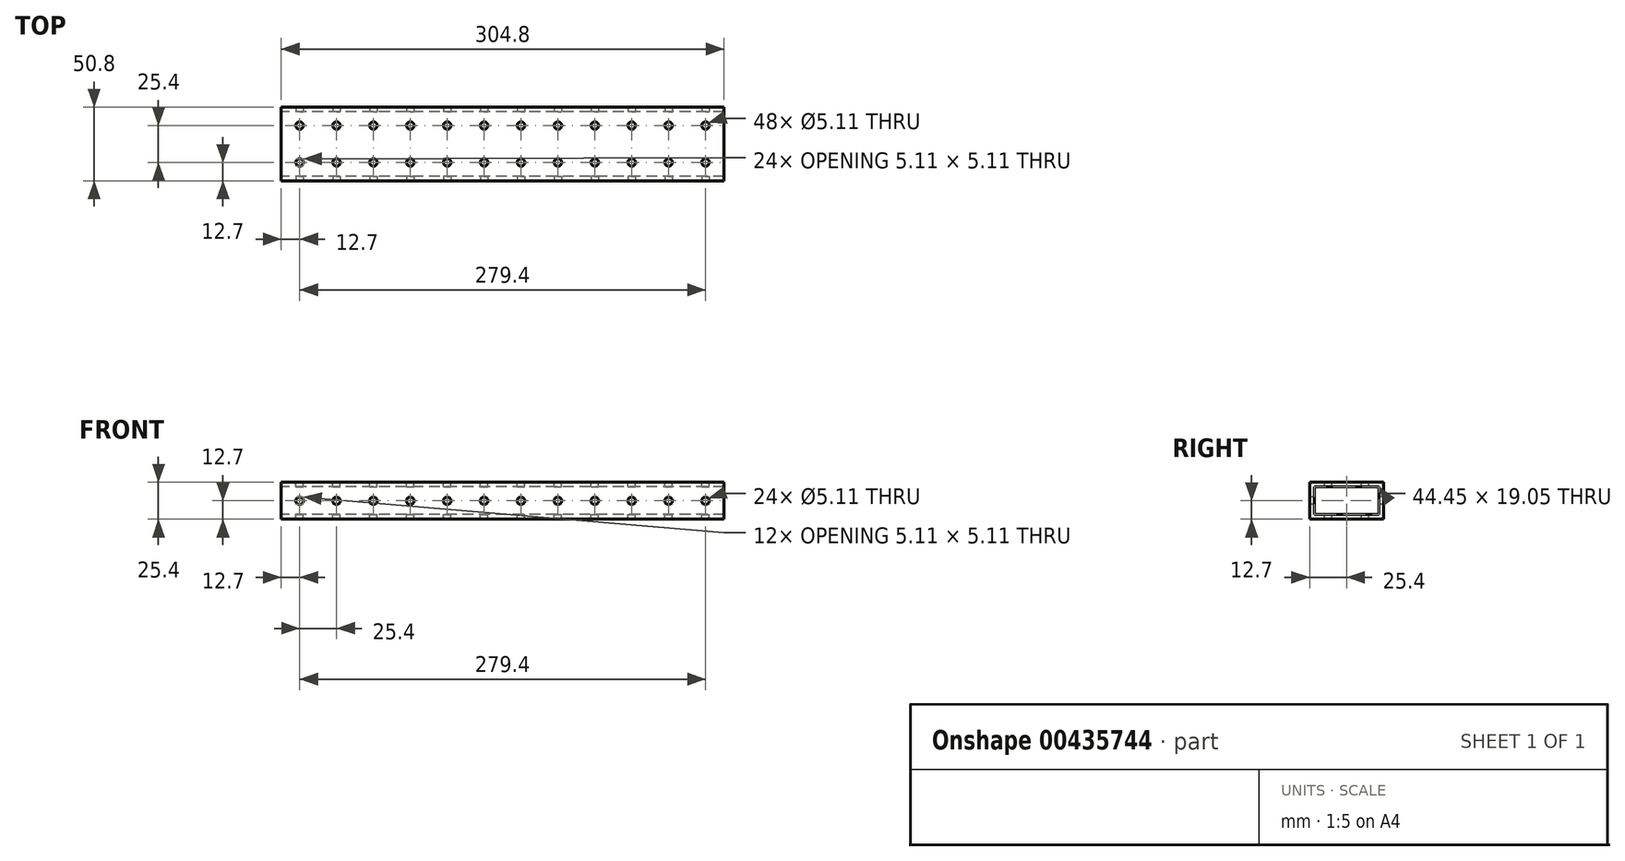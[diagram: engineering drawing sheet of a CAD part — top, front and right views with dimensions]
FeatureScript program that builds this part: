
annotation { "Feature Type Name" : "Feature", "Feature Type Description" : "" }
export const myFeature = defineFeature(function(context is Context, id is Id, definition is map)
    precondition{}
    {
        {
            var Q0;
            Q0=qCreatedBy(makeId("Right.planeOp"),FACE);
            var sketch = newSketch(context, id + "F0", { "sketchPlane" : qUnion([Q0])});
            skLineSegment(sketch, "E0.bottom", {"start": v(-25.4, -12.7) * mm, "end": v(25.4, -12.7) * mm});
            skLineSegment(sketch, "E0.top", {"start": v(-25.4, 12.7) * mm, "end": v(25.4, 12.7) * mm});
            skLineSegment(sketch, "E0.left", {"start": v(-25.4, -12.7) * mm, "end": v(-25.4, 12.7) * mm});
            skLineSegment(sketch, "E0.right", {"start": v(25.4, -12.7) * mm, "end": v(25.4, 12.7) * mm});
            skPoint(sketch, "E0.middle", {"position": v(0, 0) * mm});
            skLineSegment(sketch, "E1.bottom", {"start": v(22.23, 9.53) * mm, "end": v(-22.23, 9.53) * mm});
            skLineSegment(sketch, "E1.top", {"start": v(22.23, -9.53) * mm, "end": v(-22.23, -9.53) * mm});
            skLineSegment(sketch, "E1.left", {"start": v(22.23, 9.53) * mm, "end": v(22.23, -9.53) * mm});
            skLineSegment(sketch, "E1.right", {"start": v(-22.23, 9.53) * mm, "end": v(-22.23, -9.53) * mm});
            skSolve(sketch);
        }
        {
            var Q0;
            Q0=makeQuery(id+"F0.imprint","IMPRINT",FACE,{"disambiguationData":[TD([[makeQuery(id+"F0.imprint","IMPRINT",EDGE,{"derivedFrom":sQuery(id+"F0.wireOp",EDGE,"E0.bottom")}),1.0]])]});
            extrude(context, id + "F1", {"entities" : qUnion([Q0]), "depth" : 304.8 * mm});
        }
        {
            var Q0;
            Q0=makeQuery(id+"F1.opExtrude","SWEPT_FACE",FACE,{"disambiguationData":[OSD([sQuery(id+"F0.wireOp",EDGE,"E0.left")])]});
            var sketch = newSketch(context, id + "F2", { "sketchPlane" : qUnion([Q0])});
            skCircle(sketch, "E2", {"center": v(12.7, 0) * mm, "radius": 2.55 * mm});
            skCircle(sketch, "E3.1.0.0", {"center": v(38.1, 0) * mm, "radius": 2.55 * mm});
            skCircle(sketch, "E3.1.1.0", {"center": v(38.1, 0) * mm, "radius": 2.55 * mm});
            skCircle(sketch, "E3.2.0.0", {"center": v(63.5, 0) * mm, "radius": 2.55 * mm});
            skCircle(sketch, "E3.2.1.0", {"center": v(63.5, 0) * mm, "radius": 2.55 * mm});
            skCircle(sketch, "E3.3.0.0", {"center": v(88.9, 0) * mm, "radius": 2.55 * mm});
            skCircle(sketch, "E3.3.1.0", {"center": v(88.9, 0) * mm, "radius": 2.55 * mm});
            skCircle(sketch, "E3.4.0.0", {"center": v(114.3, 0) * mm, "radius": 2.55 * mm});
            skCircle(sketch, "E3.4.1.0", {"center": v(114.3, 0) * mm, "radius": 2.55 * mm});
            skCircle(sketch, "E3.5.0.0", {"center": v(139.7, 0) * mm, "radius": 2.55 * mm});
            skCircle(sketch, "E3.5.1.0", {"center": v(139.7, 0) * mm, "radius": 2.55 * mm});
            skCircle(sketch, "E3.6.0.0", {"center": v(165.1, 0) * mm, "radius": 2.55 * mm});
            skCircle(sketch, "E3.6.1.0", {"center": v(165.1, 0) * mm, "radius": 2.55 * mm});
            skCircle(sketch, "E3.7.0.0", {"center": v(190.5, 0) * mm, "radius": 2.55 * mm});
            skCircle(sketch, "E3.7.1.0", {"center": v(190.5, 0) * mm, "radius": 2.55 * mm});
            skCircle(sketch, "E3.8.0.0", {"center": v(215.9, 0) * mm, "radius": 2.55 * mm});
            skCircle(sketch, "E3.8.1.0", {"center": v(215.9, 0) * mm, "radius": 2.55 * mm});
            skCircle(sketch, "E3.9.0.0", {"center": v(241.3, 0) * mm, "radius": 2.55 * mm});
            skCircle(sketch, "E3.9.1.0", {"center": v(241.3, 0) * mm, "radius": 2.55 * mm});
            skCircle(sketch, "E3.10.0.0", {"center": v(266.7, 0) * mm, "radius": 2.55 * mm});
            skCircle(sketch, "E3.10.1.0", {"center": v(266.7, 0) * mm, "radius": 2.55 * mm});
            skCircle(sketch, "E3.11.0.0", {"center": v(292.1, 0) * mm, "radius": 2.55 * mm});
            skCircle(sketch, "E3.11.1.0", {"center": v(292.1, 0) * mm, "radius": 2.55 * mm});
            skLineSegment(sketch, "E3.direction1", {"start": v(12.7, 0) * mm, "end": v(38.1, 0) * mm, "construction": true});
            skLineSegment(sketch, "E3.direction2", {"start": v(12.7, 0) * mm, "end": v(12.7, 0) * mm});
            skSolve(sketch);
        }
        {
            var Q0;
            Q0=sQuery(id+"F2.wireOp",VERTEX,"E3.8.0.0.center");
            var Q1;
            Q1=sQuery(id+"F2.wireOp",VERTEX,"E3.16.0.0.center");
            var Q2;
            Q2=sQuery(id+"F2.wireOp",VERTEX,"E3.2.1.0.center");
            var Q3;
            Q3=sQuery(id+"F2.wireOp",VERTEX,"E3.3.0.0.center");
            var Q4;
            Q4=sQuery(id+"F2.wireOp",VERTEX,"E3.6.1.0.center");
            var Q5;
            Q5=sQuery(id+"F2.wireOp",VERTEX,"E3.direction1.end");
            var Q6;
            Q6=sQuery(id+"F2.wireOp",VERTEX,"E2.center");
            var Q7;
            Q7=sQuery(id+"F2.wireOp",VERTEX,"E3.4.0.0.center");
            var Q8;
            Q8=sQuery(id+"F2.wireOp",VERTEX,"E3.11.0.0.center");
            var Q9;
            Q9=sQuery(id+"F2.wireOp",VERTEX,"E3.19.0.0.center");
            var Q10;
            Q10=sQuery(id+"F2.wireOp",VERTEX,"E3.5.0.0.center");
            var Q11;
            Q11=sQuery(id+"F2.wireOp",VERTEX,"E3.22.0.0.center");
            var Q12;
            Q12=sQuery(id+"F2.wireOp",VERTEX,"E3.14.0.0.center");
            var Q13;
            Q13=sQuery(id+"F2.wireOp",VERTEX,"E3.21.1.0.center");
            var Q14;
            Q14=sQuery(id+"F2.wireOp",VERTEX,"E3.9.0.0.center");
            var Q15;
            Q15=sQuery(id+"F2.wireOp",VERTEX,"E3.17.0.0.center");
            var Q16;
            Q16=sQuery(id+"F2.wireOp",VERTEX,"E3.13.1.0.center");
            var Q17;
            Q17=sQuery(id+"F2.wireOp",VERTEX,"E3.7.0.0.center");
            var Q18;
            Q18=sQuery(id+"F2.wireOp",VERTEX,"E3.15.0.0.center");
            var Q19;
            Q19=sQuery(id+"F2.wireOp",VERTEX,"E3.12.1.0.center");
            var Q20;
            Q20=sQuery(id+"F2.wireOp",VERTEX,"E3.20.1.0.center");
            var Q21;
            Q21=sQuery(id+"F2.wireOp",VERTEX,"E3.10.1.0.center");
            var Q22;
            Q22=sQuery(id+"F2.wireOp",VERTEX,"E3.18.1.0.center");
            var Q23;
            Q23=makeQuery(id+"F1.opExtrude","SWEPT_BODY",BODY,{"disambiguationData":[OSD([sQuery(id+"F0.wireOp",EDGE,"E0.bottom"),sQuery(id+"F0.wireOp",EDGE,"E0.top"),sQuery(id+"F0.wireOp",EDGE,"E0.left"),sQuery(id+"F0.wireOp",EDGE,"E0.right"),sQuery(id+"F0.wireOp",EDGE,"E1.bottom"),sQuery(id+"F0.wireOp",EDGE,"E1.top"),sQuery(id+"F0.wireOp",EDGE,"E1.left"),sQuery(id+"F0.wireOp",EDGE,"E1.right")])]});
            hole(context, id + "F3", {"style" : HoleStyle.SIMPLE, "endStyle" : HoleEndStyle.THROUGH, "holeDiameter" : 5.1 * mm, "isTappedThrough" : true, "tappedDepth" : 12.7 * mm, "tapClearance" : 3, "locations" : qUnion([Q0, Q1, Q2, Q3, Q4, Q5, Q6, Q7, Q8, Q9, Q10, Q11, Q12, Q13, Q14, Q15, Q16, Q17, Q18, Q19, Q20, Q21, Q22]), "scope" : qUnion([Q23])});
        }
        {
            var Q0;
            Q0=makeQuery(id+"F1.opExtrude","SWEPT_FACE",FACE,{"disambiguationData":[OSD([sQuery(id+"F0.wireOp",EDGE,"E0.top")])]});
            var sketch = newSketch(context, id + "F4", { "sketchPlane" : qUnion([Q0])});
            skCircle(sketch, "E4", {"center": v(292.1, 12.7) * mm, "radius": 2.55 * mm});
            skCircle(sketch, "E5.0.1.0", {"center": v(292.1, -12.7) * mm, "radius": 2.55 * mm});
            skLineSegment(sketch, "E5.direction1", {"start": v(292.1, 12.7) * mm, "end": v(266.7, 12.7) * mm, "construction": true});
            skLineSegment(sketch, "E5.direction2", {"start": v(292.1, 12.7) * mm, "end": v(292.1, -12.7) * mm, "construction": true});
            skCircle(sketch, "E6.0.1.0", {"center": v(266.7, 12.7) * mm, "radius": 2.55 * mm});
            skCircle(sketch, "E6.0.1.1", {"center": v(266.7, -12.7) * mm, "radius": 2.55 * mm});
            skCircle(sketch, "E6.0.2.0", {"center": v(241.3, 12.7) * mm, "radius": 2.55 * mm});
            skCircle(sketch, "E6.0.2.1", {"center": v(241.3, -12.7) * mm, "radius": 2.55 * mm});
            skCircle(sketch, "E6.0.3.0", {"center": v(215.9, 12.7) * mm, "radius": 2.55 * mm});
            skCircle(sketch, "E6.0.3.1", {"center": v(215.9, -12.7) * mm, "radius": 2.55 * mm});
            skCircle(sketch, "E6.0.4.0", {"center": v(190.5, 12.7) * mm, "radius": 2.55 * mm});
            skCircle(sketch, "E6.0.4.1", {"center": v(190.5, -12.7) * mm, "radius": 2.55 * mm});
            skCircle(sketch, "E6.0.5.0", {"center": v(165.1, 12.7) * mm, "radius": 2.55 * mm});
            skCircle(sketch, "E6.0.5.1", {"center": v(165.1, -12.7) * mm, "radius": 2.55 * mm});
            skCircle(sketch, "E6.0.6.0", {"center": v(139.7, 12.7) * mm, "radius": 2.55 * mm});
            skCircle(sketch, "E6.0.6.1", {"center": v(139.7, -12.7) * mm, "radius": 2.55 * mm});
            skCircle(sketch, "E6.0.7.0", {"center": v(114.3, 12.7) * mm, "radius": 2.55 * mm});
            skCircle(sketch, "E6.0.7.1", {"center": v(114.3, -12.7) * mm, "radius": 2.55 * mm});
            skCircle(sketch, "E6.0.8.0", {"center": v(88.9, 12.7) * mm, "radius": 2.55 * mm});
            skCircle(sketch, "E6.0.8.1", {"center": v(88.9, -12.7) * mm, "radius": 2.55 * mm});
            skCircle(sketch, "E6.0.9.0", {"center": v(63.5, 12.7) * mm, "radius": 2.55 * mm});
            skCircle(sketch, "E6.0.9.1", {"center": v(63.5, -12.7) * mm, "radius": 2.55 * mm});
            skCircle(sketch, "E7.0.10.0", {"center": v(38.1, 12.7) * mm, "radius": 2.55 * mm});
            skCircle(sketch, "E7.0.10.1", {"center": v(38.1, -12.7) * mm, "radius": 2.55 * mm});
            skCircle(sketch, "E7.0.11.0", {"center": v(12.7, 12.7) * mm, "radius": 2.55 * mm});
            skCircle(sketch, "E7.0.11.1", {"center": v(12.7, -12.7) * mm, "radius": 2.55 * mm});
            skSolve(sketch);
        }
        {
            var Q0;
            Q0=sQuery(id+"F4.wireOp",VERTEX,"E6.0.7.0.center");
            var Q1;
            Q1=sQuery(id+"F4.wireOp",VERTEX,"E7.0.10.1.center");
            var Q2;
            Q2=sQuery(id+"F4.wireOp",VERTEX,"E6.0.9.0.center");
            var Q3;
            Q3=sQuery(id+"F4.wireOp",VERTEX,"E7.0.10.0.center");
            var Q4;
            Q4=sQuery(id+"F4.wireOp",VERTEX,"E6.0.8.1.center");
            var Q5;
            Q5=sQuery(id+"F4.wireOp",VERTEX,"E6.0.1.1.center");
            var Q6;
            Q6=sQuery(id+"F4.wireOp",VERTEX,"E6.0.3.0.center");
            var Q7;
            Q7=sQuery(id+"F4.wireOp",VERTEX,"E6.0.6.1.center");
            var Q8;
            Q8=sQuery(id+"F4.wireOp",VERTEX,"E6.0.9.1.center");
            var Q9;
            Q9=sQuery(id+"F4.wireOp",VERTEX,"E6.0.4.0.center");
            var Q10;
            Q10=sQuery(id+"F4.wireOp",VERTEX,"E6.0.2.1.center");
            var Q11;
            Q11=sQuery(id+"F4.wireOp",VERTEX,"E6.0.7.1.center");
            var Q12;
            Q12=sQuery(id+"F4.wireOp",VERTEX,"E7.0.11.0.center");
            var Q13;
            Q13=sQuery(id+"F4.wireOp",VERTEX,"E4.center");
            var Q14;
            Q14=sQuery(id+"F4.wireOp",VERTEX,"E7.0.11.1.center");
            var Q15;
            Q15=sQuery(id+"F4.wireOp",VERTEX,"E6.0.4.1.center");
            var Q16;
            Q16=sQuery(id+"F4.wireOp",VERTEX,"E6.0.8.0.center");
            var Q17;
            Q17=sQuery(id+"F4.wireOp",VERTEX,"E6.0.2.0.center");
            var Q18;
            Q18=sQuery(id+"F4.wireOp",VERTEX,"E6.0.5.1.center");
            var Q19;
            Q19=sQuery(id+"F4.wireOp",VERTEX,"E6.0.5.0.center");
            var Q20;
            Q20=sQuery(id+"F4.wireOp",VERTEX,"E6.0.6.0.center");
            var Q21;
            Q21=sQuery(id+"F4.wireOp",VERTEX,"E6.0.1.0.center");
            var Q22;
            Q22=sQuery(id+"F4.wireOp",VERTEX,"E5.0.1.0.center");
            var Q23;
            Q23=sQuery(id+"F4.wireOp",VERTEX,"E6.0.3.1.center");
            var Q24;
            Q24=makeQuery(id+"F1.opExtrude","SWEPT_BODY",BODY,{"disambiguationData":[OSD([sQuery(id+"F0.wireOp",EDGE,"E0.bottom"),sQuery(id+"F0.wireOp",EDGE,"E0.top"),sQuery(id+"F0.wireOp",EDGE,"E0.left"),sQuery(id+"F0.wireOp",EDGE,"E0.right"),sQuery(id+"F0.wireOp",EDGE,"E1.bottom"),sQuery(id+"F0.wireOp",EDGE,"E1.top"),sQuery(id+"F0.wireOp",EDGE,"E1.left"),sQuery(id+"F0.wireOp",EDGE,"E1.right")])]});
            hole(context, id + "F5", {"style" : HoleStyle.SIMPLE, "endStyle" : HoleEndStyle.THROUGH, "holeDiameter" : 5.1 * mm, "isTappedThrough" : true, "tappedDepth" : 12.7 * mm, "tapClearance" : 3, "locations" : qUnion([Q0, Q1, Q2, Q3, Q4, Q5, Q6, Q7, Q8, Q9, Q10, Q11, Q12, Q13, Q14, Q15, Q16, Q17, Q18, Q19, Q20, Q21, Q22, Q23]), "scope" : qUnion([Q24])});
        }
    });
